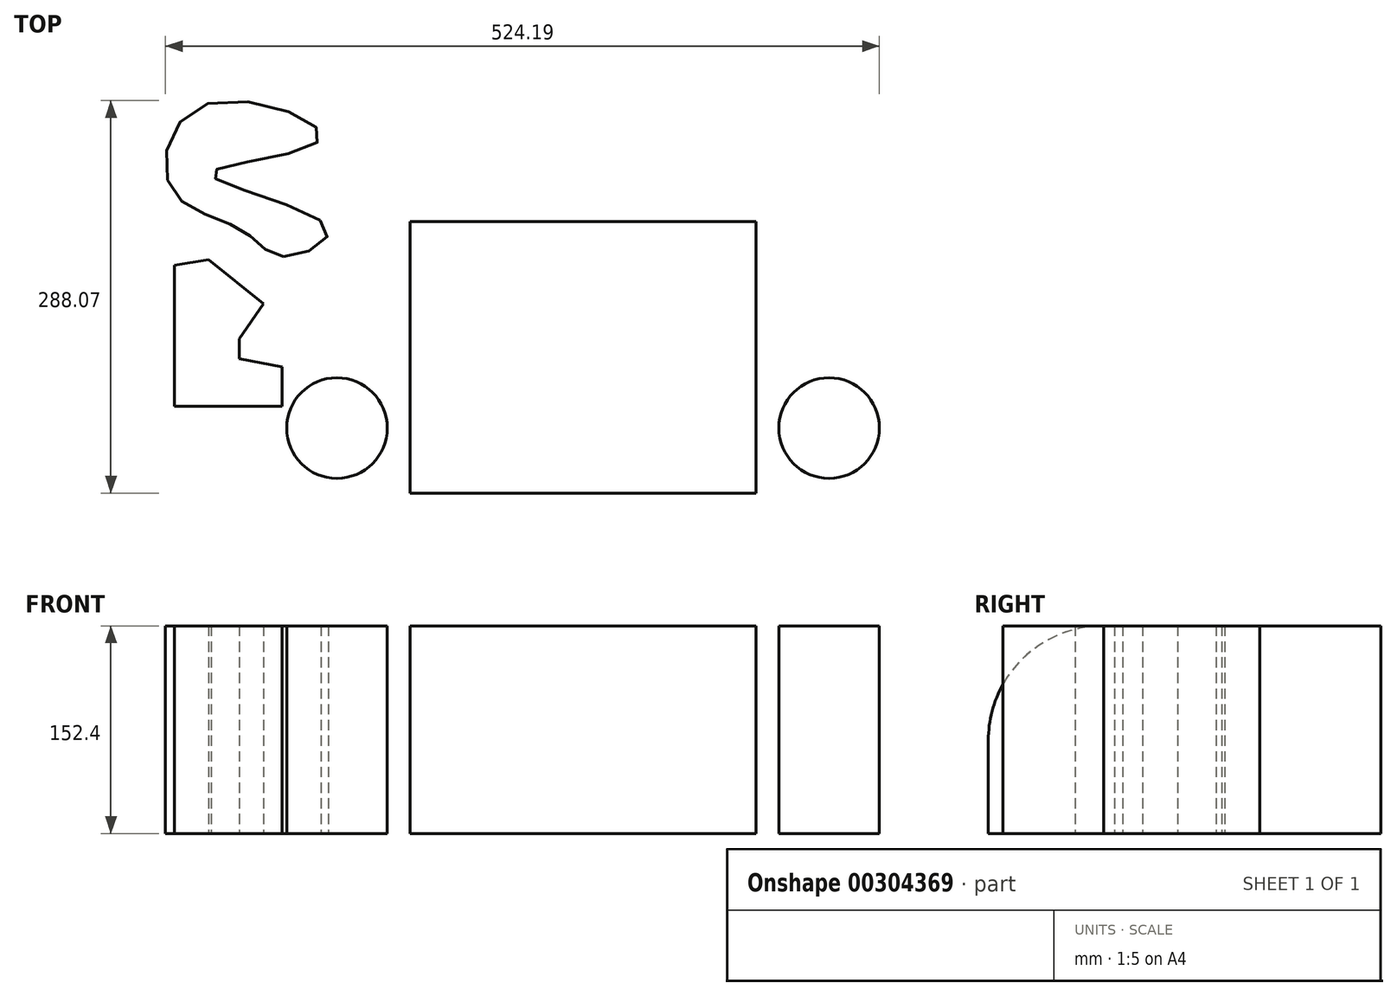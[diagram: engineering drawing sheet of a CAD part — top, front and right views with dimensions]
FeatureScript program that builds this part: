
annotation { "Feature Type Name" : "Feature", "Feature Type Description" : "" }
export const myFeature = defineFeature(function(context is Context, id is Id, definition is map)
    precondition{}
    {
        {
            var Q0;
            Q0=qCreatedBy(makeId("Top.planeOp"),FACE);
            var sketch = newSketch(context, id + "F0", { "sketchPlane" : qUnion([Q0])});
            skLineSegment(sketch, "E0.bottom", {"start": v(-127, 99.71) * mm, "end": v(127, 99.71) * mm});
            skLineSegment(sketch, "E0.top", {"start": v(-127, -99.71) * mm, "end": v(127, -99.71) * mm});
            skLineSegment(sketch, "E0.left", {"start": v(-127, 99.71) * mm, "end": v(-127, -99.71) * mm});
            skLineSegment(sketch, "E0.right", {"start": v(127, 99.71) * mm, "end": v(127, -99.71) * mm});
            skPoint(sketch, "E0.middle", {"position": v(0, 0) * mm});
            skCircle(sketch, "E1", {"center": v(180.68, -52) * mm, "radius": 36.92 * mm});
            skLineSegment(sketch, "E2", {"start": v(0, 0) * mm, "end": v(0, 164.64) * mm, "construction": true});
            skPoint(sketch, "E2.endSnap0", {"position": v(0, 99.71) * mm});
            skCircle(sketch, "E3.MirrorC", {"center": v(-180.68, -52) * mm, "radius": 36.92 * mm});
            skLineSegment(sketch, "E4", {"start": v(-300, 67.52) * mm, "end": v(-300, -35.96) * mm});
            skLineSegment(sketch, "E5", {"start": v(-300, -35.96) * mm, "end": v(-220.91, -35.96) * mm});
            skLineSegment(sketch, "E6", {"start": v(-220.91, -35.96) * mm, "end": v(-220.91, -6.96) * mm});
            skLineSegment(sketch, "E7", {"start": v(-220.91, -6.96) * mm, "end": v(-252.55, -1.06) * mm});
            skLineSegment(sketch, "E8", {"start": v(-252.55, -1.06) * mm, "end": v(-252.55, 13.48) * mm});
            skLineSegment(sketch, "E9", {"start": v(-252.55, 13.48) * mm, "end": v(-234.75, 39.18) * mm});
            skLineSegment(sketch, "E10", {"start": v(-234.75, 39.18) * mm, "end": v(-246.38, 48.58) * mm});
            skLineSegment(sketch, "E11", {"start": v(-246.38, 48.58) * mm, "end": v(-256.99, 57.16) * mm});
            skLineSegment(sketch, "E12", {"start": v(-256.99, 57.16) * mm, "end": v(-274.95, 71.68) * mm});
            skLineSegment(sketch, "E13", {"start": v(-274.95, 71.68) * mm, "end": v(-300, 67.52) * mm});
            skFitSpline(sketch, "E14", {"points": [v(-220.08, 74) * mm, v(-187.67, 95.01) * mm, v(-272.9, 134.63) * mm, v(-193.07, 159.84) * mm, v(-277.1, 185.65) * mm, v(-301.72, 122.63) * mm, v(-250.1, 93.21) * mm, v(-220.08, 74) * mm]});
            skSolve(sketch);
        }
        {
            var Q0;
            Q0 = qSketchRegion(id + "F0", true);
            extrude(context, id + "F1", {"entities" : qUnion([Q0]), "depth" : 127 * mm, "hasSecondDirection" : true, "secondDirectionOppositeDirection" : true, "secondDirectionDepth" : 25.4 * mm});
        }
        {
            var Q0;
            Q0=makeQuery(id+"F1.opExtrude","CAP_EDGE",EDGE,{"disambiguationData":[OSD([sQuery(id+"F0.wireOp",EDGE,"E0.top")])],"isStart":false});
            fillet(context, id + "F2", {"entities" : qUnion([Q0]), "radius" : 84 * mm, "tangentPropagation" : true, "allowEdgeOverflow" : false});
        }
    });
